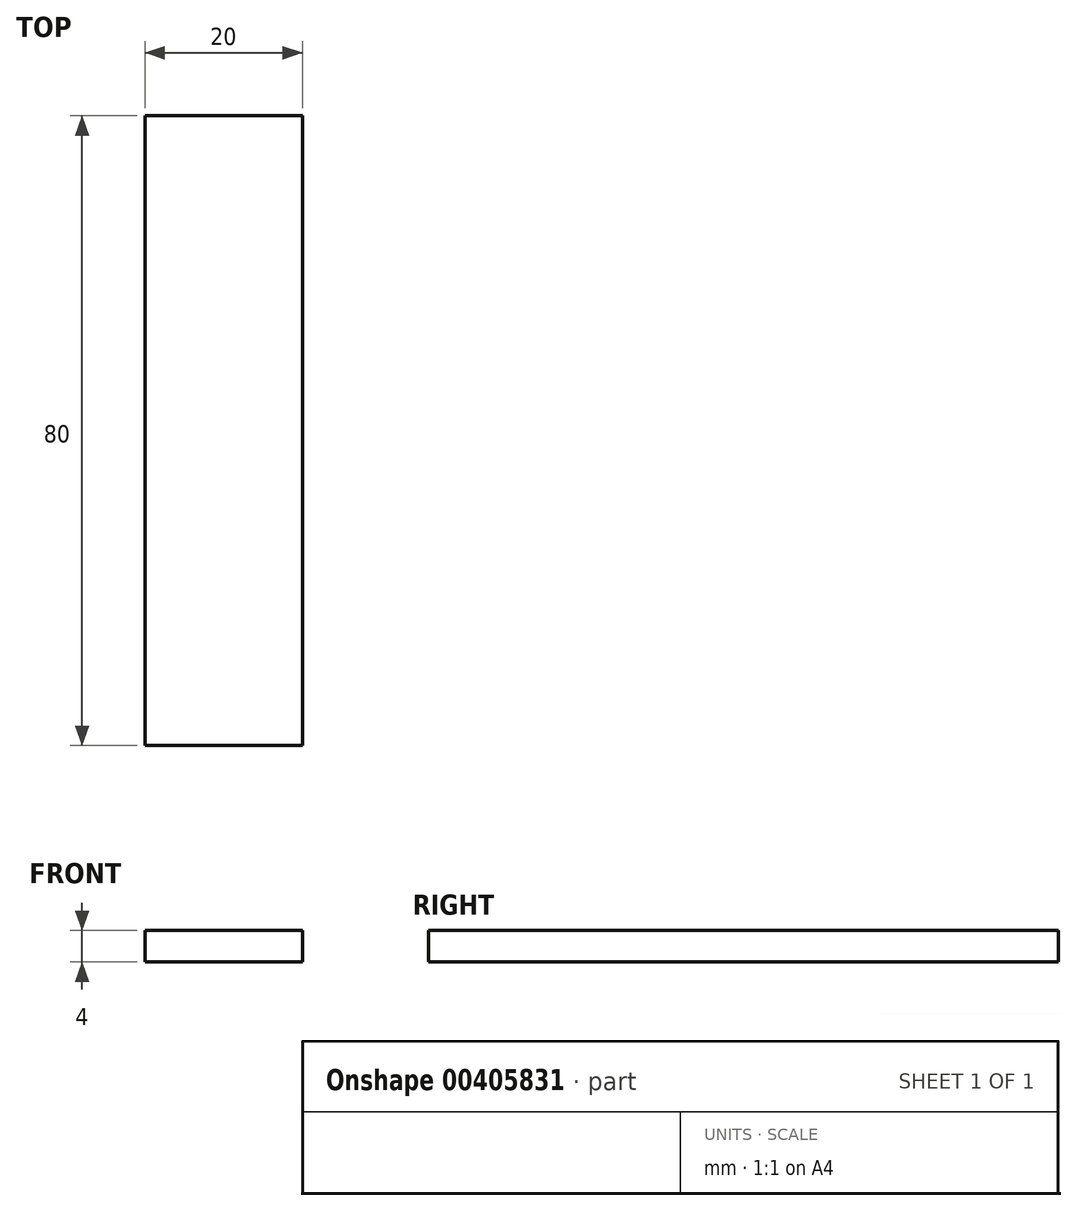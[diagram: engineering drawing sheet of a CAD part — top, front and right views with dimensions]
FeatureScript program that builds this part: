
annotation { "Feature Type Name" : "Feature", "Feature Type Description" : "" }
export const myFeature = defineFeature(function(context is Context, id is Id, definition is map)
    precondition{}
    {
        {
            var Q0;
            Q0=qCreatedBy(makeId("Top.planeOp"),FACE);
            var sketch = newSketch(context, id + "F0", { "sketchPlane" : qUnion([Q0])});
            skLineSegment(sketch, "E0.bottom", {"start": v(10, -40) * mm, "end": v(-10, -40) * mm});
            skLineSegment(sketch, "E0.top", {"start": v(10, 40) * mm, "end": v(-10, 40) * mm});
            skLineSegment(sketch, "E0.left", {"start": v(10, -40) * mm, "end": v(10, 40) * mm});
            skLineSegment(sketch, "E0.right", {"start": v(-10, -40) * mm, "end": v(-10, 40) * mm});
            skPoint(sketch, "E0.middle", {"position": v(0, 0) * mm});
            skSolve(sketch);
        }
        {
            var Q0;
            Q0=makeQuery(id+"F0.imprint","IMPRINT",FACE,{"disambiguationData":[TD([[makeQuery(id+"F0.imprint","IMPRINT",EDGE,{"derivedFrom":sQuery(id+"F0.wireOp",EDGE,"E0.bottom")}),-1.0]])]});
            extrude(context, id + "F1", {"entities" : qUnion([Q0]), "depth" : 4 * mm});
        }
    });
